# Revit family: RN 82230 Optipress-Aquaplus-Valvola di distribuzione
name_source: partatom
category: Rohrzubehör
units: mm (PartAtom-declared; Revit-internal decimal feet)

## family parameters
Arbeitsebenenbasiert = Nein
Beim Laden mit Abzugskörper schneiden = Nein
Bemaßung runder Anschluss = Durchmesser verwenden
Gemeinsam genutzt = Nein
Immer vertikal = Ja
Teiletyp = Ventil - Zerlegung in

## types (14) — shared parameters
1.010.00.2 Blattnummer der Richtlinie = 17
1.010.00.3 Ausgabedatum (Monat) der Richtlinie = 201601
1.010.00.4 Herstellername = R. Nussbaum AG
1.010.00.5 Revisionsdatum der Datei = 20190528
1.010.00.6 Webadresse des Herstellers = http://www.nussbaum.ch
1.100.00.3 Sortiernummer für Anzeigereihenfolge = 1
1.100.00.4 Produktbezeichnung = Absperrarmaturen
1.960/3L.00.8 Link (URL) = https://www.nussbaum.ch
17.700.00.4 Armaturentyp = 1
17.700.00.7 Maximale Betriebstemperatur TB [°C] = 90
17.700.00.8 Maximaler Betriebsdruck (Arbeitsdruck) ps [1.0 · 105 Pa] = 16
Connector Visibility = Nein
EnclosingSpace Visibility = Nein
Hersteller = R. Nussbauzm AG
URL = https://www.nussbaum.ch

## per-type parameters (varying)
- DN 20 1: 1.800.00.3 TGA-Nummer=00110000000000000000000000000200700000000000000001???00000; 1.810.00.3 Hersteller-Bestellnummer=82230.4; 1.810.00.4 DATANORM-Nummer=82230.4; 1.810.00.6 GTIN-Nummer=7612945729064; 17.700.00.30 Produktbeschreibung=82230.40, Optipress-Aquaplus-Batterieventil, ohne Anschlussverschraubung, DN=20; 17.700.00.5 Nennweite DN=20; 17.700.00.6 kvs-Wert [m3/h]=22.84; CONNECTOR0_DIAMETER_dX_0r=25 mm  [stored 0.082021 ft]; CONNECTOR0_dX_00=54 mm; CONNECTOR0_dX_01=31 mm; CONNECTOR0_ref_dX=31 mm; CONNECTOR1_DIAMETER_dX_0r=25 mm  [stored 0.082021 ft]; CONNECTOR1_dX_00=31 mm; CONNECTOR1_dX_01=54 mm; CONNECTOR1_ref_dX=31 mm; CONNECTOR2_DIAMETER_dZ_0r=25 mm  [stored 0.082021 ft]; CONNECTOR2_dZ_00=48 mm; CONNECTOR2_dZ_01=60 mm  [stored 0.19685 ft]; CONNECTOR2_ref_dZ=48 mm; Modell=82230.4; R. Nussbaum AG 82230.40 de Visibility=Ja; R. Nussbaum AG 82230.41 de Visibility=Nein; R. Nussbaum AG 82230.42 de Visibility=Nein; R. Nussbaum AG 82230.43 de Visibility=Nein; R. Nussbaum AG 82230.44 de Visibility=Nein; R. Nussbaum AG 82230.45 de Visibility=Nein; R. Nussbaum AG 82230.46 de Visibility=Nein; R. Nussbaum AG 82230.47 de Visibility=Nein; R. Nussbaum AG 82230.48 de Visibility=Nein; R. Nussbaum AG 82230.49 de Visibility=Nein; R. Nussbaum AG 82230.50 de Visibility=Nein; R. Nussbaum AG 82230.51 de Visibility=Nein; R. Nussbaum AG 82230.52 de Visibility=Nein; R. Nussbaum AG 82230.53 de Visibility=Nein; Typenkommentare=Optipress-Aquaplus-Valvola di distribuzioneDN 20 1
- DN 25: 1.800.00.3 TGA-Nummer=00110000000000000000000000000200700000000000000002???00000; 1.810.00.3 Hersteller-Bestellnummer=82230.41; 1.810.00.4 DATANORM-Nummer=82230.41; 1.810.00.6 GTIN-Nummer=7612945729118; 17.700.00.30 Produktbeschreibung=82230.41, Optipress-Aquaplus-Batterieventil, ohne Anschlussverschraubung, DN=25; 17.700.00.5 Nennweite DN=25; 17.700.00.6 kvs-Wert [m3/h]=22.84; CONNECTOR0_DIAMETER_dX_0r=25 mm  [stored 0.082021 ft]; CONNECTOR0_dX_00=54 mm; CONNECTOR0_dX_01=31 mm; CONNECTOR0_ref_dX=31 mm; CONNECTOR1_DIAMETER_dX_0r=25 mm  [stored 0.082021 ft]; CONNECTOR1_dX_00=31 mm; CONNECTOR1_dX_01=54 mm; CONNECTOR1_ref_dX=31 mm; CONNECTOR2_DIAMETER_dZ_0r=25 mm  [stored 0.082021 ft]; CONNECTOR2_dZ_00=48 mm; CONNECTOR2_dZ_01=60 mm  [stored 0.19685 ft]; CONNECTOR2_ref_dZ=48 mm; Modell=82230.41; R. Nussbaum AG 82230.40 de Visibility=Nein; R. Nussbaum AG 82230.41 de Visibility=Ja; R. Nussbaum AG 82230.42 de Visibility=Nein; R. Nussbaum AG 82230.43 de Visibility=Nein; R. Nussbaum AG 82230.44 de Visibility=Nein; R. Nussbaum AG 82230.45 de Visibility=Nein; R. Nussbaum AG 82230.46 de Visibility=Nein; R. Nussbaum AG 82230.47 de Visibility=Nein; R. Nussbaum AG 82230.48 de Visibility=Nein; R. Nussbaum AG 82230.49 de Visibility=Nein; R. Nussbaum AG 82230.50 de Visibility=Nein; R. Nussbaum AG 82230.51 de Visibility=Nein; R. Nussbaum AG 82230.52 de Visibility=Nein; R. Nussbaum AG 82230.53 de Visibility=Nein; Typenkommentare=Optipress-Aquaplus-Valvola di distribuzioneDN 25
- DN 20 2: 1.800.00.3 TGA-Nummer=00110000000000000000000000000200700000000000000003???00000; 1.810.00.3 Hersteller-Bestellnummer=82230.42; 1.810.00.4 DATANORM-Nummer=82230.42; 1.810.00.6 GTIN-Nummer=7612945729071; 17.700.00.30 Produktbeschreibung=82230.42, Optipress-Aquaplus-Batterieventil, ohne Anschlussverschraubung, DN=20; 17.700.00.5 Nennweite DN=20; 17.700.00.6 kvs-Wert [m3/h]=43.05; CONNECTOR0_DIAMETER_dX_0r=32 mm; CONNECTOR0_dX_00=56 mm; CONNECTOR0_dX_01=31 mm; CONNECTOR0_ref_dX=31 mm; CONNECTOR1_DIAMETER_dX_0r=32 mm; CONNECTOR1_dX_00=31 mm; CONNECTOR1_dX_01=56 mm; CONNECTOR1_ref_dX=31 mm; CONNECTOR2_DIAMETER_dZ_0r=25 mm  [stored 0.082021 ft]; CONNECTOR2_dZ_00=50 mm  [stored 0.164042 ft]; CONNECTOR2_dZ_01=62 mm  [stored 0.203412 ft]; CONNECTOR2_ref_dZ=50 mm  [stored 0.164042 ft]; Modell=82230.42; R. Nussbaum AG 82230.40 de Visibility=Nein; R. Nussbaum AG 82230.41 de Visibility=Nein; R. Nussbaum AG 82230.42 de Visibility=Ja; R. Nussbaum AG 82230.43 de Visibility=Nein; R. Nussbaum AG 82230.44 de Visibility=Nein; R. Nussbaum AG 82230.45 de Visibility=Nein; R. Nussbaum AG 82230.46 de Visibility=Nein; R. Nussbaum AG 82230.47 de Visibility=Nein; R. Nussbaum AG 82230.48 de Visibility=Nein; R. Nussbaum AG 82230.49 de Visibility=Nein; R. Nussbaum AG 82230.50 de Visibility=Nein; R. Nussbaum AG 82230.51 de Visibility=Nein; R. Nussbaum AG 82230.52 de Visibility=Nein; R. Nussbaum AG 82230.53 de Visibility=Nein; Typenkommentare=Optipress-Aquaplus-Valvola di distribuzioneDN 20 2
- DN 25 1: 1.800.00.3 TGA-Nummer=00110000000000000000000000000200700000000000000004???00000; 1.810.00.3 Hersteller-Bestellnummer=82230.43; 1.810.00.4 DATANORM-Nummer=82230.43; 1.810.00.6 GTIN-Nummer=7612945729125; 17.700.00.30 Produktbeschreibung=82230.43, Optipress-Aquaplus-Batterieventil, ohne Anschlussverschraubung, DN=25; 17.700.00.5 Nennweite DN=25; 17.700.00.6 kvs-Wert [m3/h]=43.05; CONNECTOR0_DIAMETER_dX_0r=32 mm; CONNECTOR0_dX_00=56 mm; CONNECTOR0_dX_01=31 mm; CONNECTOR0_ref_dX=31 mm; CONNECTOR1_DIAMETER_dX_0r=32 mm; CONNECTOR1_dX_00=31 mm; CONNECTOR1_dX_01=56 mm; CONNECTOR1_ref_dX=31 mm; CONNECTOR2_DIAMETER_dZ_0r=25 mm  [stored 0.082021 ft]; CONNECTOR2_dZ_00=50 mm  [stored 0.164042 ft]; CONNECTOR2_dZ_01=62 mm  [stored 0.203412 ft]; CONNECTOR2_ref_dZ=50 mm  [stored 0.164042 ft]; Modell=82230.43; R. Nussbaum AG 82230.40 de Visibility=Nein; R. Nussbaum AG 82230.41 de Visibility=Nein; R. Nussbaum AG 82230.42 de Visibility=Nein; R. Nussbaum AG 82230.43 de Visibility=Ja; R. Nussbaum AG 82230.44 de Visibility=Nein; R. Nussbaum AG 82230.45 de Visibility=Nein; R. Nussbaum AG 82230.46 de Visibility=Nein; R. Nussbaum AG 82230.47 de Visibility=Nein; R. Nussbaum AG 82230.48 de Visibility=Nein; R. Nussbaum AG 82230.49 de Visibility=Nein; R. Nussbaum AG 82230.50 de Visibility=Nein; R. Nussbaum AG 82230.51 de Visibility=Nein; R. Nussbaum AG 82230.52 de Visibility=Nein; R. Nussbaum AG 82230.53 de Visibility=Nein; Typenkommentare=Optipress-Aquaplus-Valvola di distribuzioneDN 25 1
- DN 32: 1.800.00.3 TGA-Nummer=00110000000000000000000000000200700000000000000005???00000; 1.810.00.3 Hersteller-Bestellnummer=82230.44; 1.810.00.4 DATANORM-Nummer=82230.44; 1.810.00.6 GTIN-Nummer=7612945729088; 17.700.00.30 Produktbeschreibung=82230.44, Optipress-Aquaplus-Batterieventil, ohne Anschlussverschraubung, DN=32; 17.700.00.5 Nennweite DN=32; 17.700.00.6 kvs-Wert [m3/h]=43.05; CONNECTOR0_DIAMETER_dX_0r=32 mm; CONNECTOR0_dX_00=56 mm; CONNECTOR0_dX_01=31 mm; CONNECTOR0_ref_dX=31 mm; CONNECTOR1_DIAMETER_dX_0r=32 mm; CONNECTOR1_dX_00=31 mm; CONNECTOR1_dX_01=56 mm; CONNECTOR1_ref_dX=31 mm; CONNECTOR2_DIAMETER_dZ_0r=32 mm; CONNECTOR2_dZ_00=49 mm; CONNECTOR2_dZ_01=62 mm  [stored 0.203412 ft]; CONNECTOR2_ref_dZ=49 mm; Modell=82230.44; R. Nussbaum AG 82230.40 de Visibility=Nein; R. Nussbaum AG 82230.41 de Visibility=Nein; R. Nussbaum AG 82230.42 de Visibility=Nein; R. Nussbaum AG 82230.43 de Visibility=Nein; R. Nussbaum AG 82230.44 de Visibility=Ja; R. Nussbaum AG 82230.45 de Visibility=Nein; R. Nussbaum AG 82230.46 de Visibility=Nein; R. Nussbaum AG 82230.47 de Visibility=Nein; R. Nussbaum AG 82230.48 de Visibility=Nein; R. Nussbaum AG 82230.49 de Visibility=Nein; R. Nussbaum AG 82230.50 de Visibility=Nein; R. Nussbaum AG 82230.51 de Visibility=Nein; R. Nussbaum AG 82230.52 de Visibility=Nein; R. Nussbaum AG 82230.53 de Visibility=Nein; Typenkommentare=Optipress-Aquaplus-Valvola di distribuzioneDN 32
- DN 20: 1.800.00.3 TGA-Nummer=00110000000000000000000000000200700000000000000006???00000; 1.810.00.3 Hersteller-Bestellnummer=82230.45; 1.810.00.4 DATANORM-Nummer=82230.45; 1.810.00.6 GTIN-Nummer=7612945729095; 17.700.00.30 Produktbeschreibung=82230.45, Optipress-Aquaplus-Batterieventil, ohne Anschlussverschraubung, DN=20; 17.700.00.5 Nennweite DN=20; 17.700.00.6 kvs-Wert [m3/h]=36.27; CONNECTOR0_DIAMETER_dX_0r=40 mm; CONNECTOR0_dX_00=66 mm  [stored 0.216535 ft]; CONNECTOR0_dX_01=30 mm  [stored 0.0984252 ft]; CONNECTOR0_ref_dX=30 mm  [stored 0.0984252 ft]; CONNECTOR1_DIAMETER_dX_0r=40 mm; CONNECTOR1_dX_00=30 mm  [stored 0.0984252 ft]; CONNECTOR1_dX_01=66 mm  [stored 0.216535 ft]; CONNECTOR1_ref_dX=30 mm  [stored 0.0984252 ft]; CONNECTOR2_DIAMETER_dZ_0r=31 mm; CONNECTOR2_dZ_00=52 mm; CONNECTOR2_dZ_01=65 mm; CONNECTOR2_ref_dZ=52 mm; Modell=82230.45; R. Nussbaum AG 82230.40 de Visibility=Nein; R. Nussbaum AG 82230.41 de Visibility=Nein; R. Nussbaum AG 82230.42 de Visibility=Nein; R. Nussbaum AG 82230.43 de Visibility=Nein; R. Nussbaum AG 82230.44 de Visibility=Nein; R. Nussbaum AG 82230.45 de Visibility=Ja; R. Nussbaum AG 82230.46 de Visibility=Nein; R. Nussbaum AG 82230.47 de Visibility=Nein; R. Nussbaum AG 82230.48 de Visibility=Nein; R. Nussbaum AG 82230.49 de Visibility=Nein; R. Nussbaum AG 82230.50 de Visibility=Nein; R. Nussbaum AG 82230.51 de Visibility=Nein; R. Nussbaum AG 82230.52 de Visibility=Nein; R. Nussbaum AG 82230.53 de Visibility=Nein; Typenkommentare=Optipress-Aquaplus-Valvola di distribuzioneDN 20
- DN 25 3: 1.800.00.3 TGA-Nummer=00110000000000000000000000000200700000000000000007???00000; 1.810.00.3 Hersteller-Bestellnummer=82230.46; 1.810.00.4 DATANORM-Nummer=82230.46; 1.810.00.6 GTIN-Nummer=7612945729132; 17.700.00.30 Produktbeschreibung=82230.46, Optipress-Aquaplus-Batterieventil, ohne Anschlussverschraubung, DN=25; 17.700.00.5 Nennweite DN=25; 17.700.00.6 kvs-Wert [m3/h]=36.27; CONNECTOR0_DIAMETER_dX_0r=40 mm; CONNECTOR0_dX_00=66 mm  [stored 0.216535 ft]; CONNECTOR0_dX_01=30 mm  [stored 0.0984252 ft]; CONNECTOR0_ref_dX=30 mm  [stored 0.0984252 ft]; CONNECTOR1_DIAMETER_dX_0r=40 mm; CONNECTOR1_dX_00=30 mm  [stored 0.0984252 ft]; CONNECTOR1_dX_01=66 mm  [stored 0.216535 ft]; CONNECTOR1_ref_dX=30 mm  [stored 0.0984252 ft]; CONNECTOR2_DIAMETER_dZ_0r=32 mm; CONNECTOR2_dZ_00=52 mm; CONNECTOR2_dZ_01=65 mm; CONNECTOR2_ref_dZ=52 mm; Modell=82230.46; R. Nussbaum AG 82230.40 de Visibility=Nein; R. Nussbaum AG 82230.41 de Visibility=Nein; R. Nussbaum AG 82230.42 de Visibility=Nein; R. Nussbaum AG 82230.43 de Visibility=Nein; R. Nussbaum AG 82230.44 de Visibility=Nein; R. Nussbaum AG 82230.45 de Visibility=Nein; R. Nussbaum AG 82230.46 de Visibility=Ja; R. Nussbaum AG 82230.47 de Visibility=Nein; R. Nussbaum AG 82230.48 de Visibility=Nein; R. Nussbaum AG 82230.49 de Visibility=Nein; R. Nussbaum AG 82230.50 de Visibility=Nein; R. Nussbaum AG 82230.51 de Visibility=Nein; R. Nussbaum AG 82230.52 de Visibility=Nein; R. Nussbaum AG 82230.53 de Visibility=Nein; Typenkommentare=Optipress-Aquaplus-Valvola di distribuzioneDN 25 3
- DN 32 2: 1.800.00.3 TGA-Nummer=00110000000000000000000000000200700000000000000008???00000; 1.810.00.3 Hersteller-Bestellnummer=82230.47; 1.810.00.4 DATANORM-Nummer=82230.47; 1.810.00.6 GTIN-Nummer=7612945729149; 17.700.00.30 Produktbeschreibung=82230.47, Optipress-Aquaplus-Batterieventil, ohne Anschlussverschraubung, DN=32; 17.700.00.5 Nennweite DN=32; 17.700.00.6 kvs-Wert [m3/h]=36.27; CONNECTOR0_DIAMETER_dX_0r=40 mm; CONNECTOR0_dX_00=66 mm  [stored 0.216535 ft]; CONNECTOR0_dX_01=30 mm  [stored 0.0984252 ft]; CONNECTOR0_ref_dX=30 mm  [stored 0.0984252 ft]; CONNECTOR1_DIAMETER_dX_0r=40 mm; CONNECTOR1_dX_00=30 mm  [stored 0.0984252 ft]; CONNECTOR1_dX_01=66 mm  [stored 0.216535 ft]; CONNECTOR1_ref_dX=30 mm  [stored 0.0984252 ft]; CONNECTOR2_DIAMETER_dZ_0r=32 mm; CONNECTOR2_dZ_00=52 mm; CONNECTOR2_dZ_01=65 mm; CONNECTOR2_ref_dZ=52 mm; Modell=82230.47; R. Nussbaum AG 82230.40 de Visibility=Nein; R. Nussbaum AG 82230.41 de Visibility=Nein; R. Nussbaum AG 82230.42 de Visibility=Nein; R. Nussbaum AG 82230.43 de Visibility=Nein; R. Nussbaum AG 82230.44 de Visibility=Nein; R. Nussbaum AG 82230.45 de Visibility=Nein; R. Nussbaum AG 82230.46 de Visibility=Nein; R. Nussbaum AG 82230.47 de Visibility=Ja; R. Nussbaum AG 82230.48 de Visibility=Nein; R. Nussbaum AG 82230.49 de Visibility=Nein; R. Nussbaum AG 82230.50 de Visibility=Nein; R. Nussbaum AG 82230.51 de Visibility=Nein; R. Nussbaum AG 82230.52 de Visibility=Nein; R. Nussbaum AG 82230.53 de Visibility=Nein; Typenkommentare=Optipress-Aquaplus-Valvola di distribuzioneDN 32 2
- DN 40 1: 1.800.00.3 TGA-Nummer=00110000000000000000000000000200700000000000000009???00000; 1.810.00.3 Hersteller-Bestellnummer=82230.48; 1.810.00.4 DATANORM-Nummer=82230.48; 1.810.00.6 GTIN-Nummer=7612945727206; 17.700.00.30 Produktbeschreibung=82230.48, Optipress-Aquaplus-Batterieventil, ohne Anschlussverschraubung, DN=40; 17.700.00.5 Nennweite DN=40; 17.700.00.6 kvs-Wert [m3/h]=36.27; CONNECTOR0_DIAMETER_dX_0r=40 mm; CONNECTOR0_dX_00=66 mm  [stored 0.216535 ft]; CONNECTOR0_dX_01=30 mm  [stored 0.0984252 ft]; CONNECTOR0_ref_dX=30 mm  [stored 0.0984252 ft]; CONNECTOR1_DIAMETER_dX_0r=40 mm; CONNECTOR1_dX_00=30 mm  [stored 0.0984252 ft]; CONNECTOR1_dX_01=66 mm  [stored 0.216535 ft]; CONNECTOR1_ref_dX=30 mm  [stored 0.0984252 ft]; CONNECTOR2_DIAMETER_dZ_0r=40 mm; CONNECTOR2_dZ_00=52 mm; CONNECTOR2_dZ_01=65 mm; CONNECTOR2_ref_dZ=52 mm; Modell=82230.48; R. Nussbaum AG 82230.40 de Visibility=Nein; R. Nussbaum AG 82230.41 de Visibility=Nein; R. Nussbaum AG 82230.42 de Visibility=Nein; R. Nussbaum AG 82230.43 de Visibility=Nein; R. Nussbaum AG 82230.44 de Visibility=Nein; R. Nussbaum AG 82230.45 de Visibility=Nein; R. Nussbaum AG 82230.46 de Visibility=Nein; R. Nussbaum AG 82230.47 de Visibility=Nein; R. Nussbaum AG 82230.48 de Visibility=Ja; R. Nussbaum AG 82230.49 de Visibility=Nein; R. Nussbaum AG 82230.50 de Visibility=Nein; R. Nussbaum AG 82230.51 de Visibility=Nein; R. Nussbaum AG 82230.52 de Visibility=Nein; R. Nussbaum AG 82230.53 de Visibility=Nein; Typenkommentare=Optipress-Aquaplus-Valvola di distribuzioneDN 40 1
- DN 20 3: 1.800.00.3 TGA-Nummer=00110000000000000000000000000200700000000000000010???00000; 1.810.00.3 Hersteller-Bestellnummer=82230.49; 1.810.00.4 DATANORM-Nummer=82230.49; 1.810.00.6 GTIN-Nummer=7612945729101; 17.700.00.30 Produktbeschreibung=82230.49, Optipress-Aquaplus-Batterieventil, ohne Anschlussverschraubung, DN=20; 17.700.00.5 Nennweite DN=20; 17.700.00.6 kvs-Wert [m3/h]=33.26; CONNECTOR0_DIAMETER_dX_0r=50 mm  [stored 0.164042 ft]; CONNECTOR0_dX_00=80 mm; CONNECTOR0_dX_01=40 mm; CONNECTOR0_ref_dX=40 mm; CONNECTOR1_DIAMETER_dX_0r=50 mm  [stored 0.164042 ft]; CONNECTOR1_dX_00=40 mm; CONNECTOR1_dX_01=80 mm; CONNECTOR1_ref_dX=40 mm; CONNECTOR2_DIAMETER_dZ_0r=52 mm; CONNECTOR2_dZ_00=60 mm  [stored 0.19685 ft]; CONNECTOR2_dZ_01=73 mm; CONNECTOR2_ref_dZ=60 mm  [stored 0.19685 ft]; Modell=82230.49; R. Nussbaum AG 82230.40 de Visibility=Nein; R. Nussbaum AG 82230.41 de Visibility=Nein; R. Nussbaum AG 82230.42 de Visibility=Nein; R. Nussbaum AG 82230.43 de Visibility=Nein; R. Nussbaum AG 82230.44 de Visibility=Nein; R. Nussbaum AG 82230.45 de Visibility=Nein; R. Nussbaum AG 82230.46 de Visibility=Nein; R. Nussbaum AG 82230.47 de Visibility=Nein; R. Nussbaum AG 82230.48 de Visibility=Nein; R. Nussbaum AG 82230.49 de Visibility=Ja; R. Nussbaum AG 82230.50 de Visibility=Nein; R. Nussbaum AG 82230.51 de Visibility=Nein; R. Nussbaum AG 82230.52 de Visibility=Nein; R. Nussbaum AG 82230.53 de Visibility=Nein; Typenkommentare=Optipress-Aquaplus-Valvola di distribuzioneDN 20 3
- DN 25 2: 1.800.00.3 TGA-Nummer=00110000000000000000000000000200700000000000000011???00000; 1.810.00.3 Hersteller-Bestellnummer=82230.5; 1.810.00.4 DATANORM-Nummer=82230.5; 1.810.00.6 GTIN-Nummer=7612945729156; 17.700.00.30 Produktbeschreibung=82230.50, Optipress-Aquaplus-Batterieventil, ohne Anschlussverschraubung, DN=25; 17.700.00.5 Nennweite DN=25; 17.700.00.6 kvs-Wert [m3/h]=33.26; CONNECTOR0_DIAMETER_dX_0r=50 mm  [stored 0.164042 ft]; CONNECTOR0_dX_00=80 mm; CONNECTOR0_dX_01=40 mm; CONNECTOR0_ref_dX=40 mm; CONNECTOR1_DIAMETER_dX_0r=50 mm  [stored 0.164042 ft]; CONNECTOR1_dX_00=40 mm; CONNECTOR1_dX_01=80 mm; CONNECTOR1_ref_dX=40 mm; CONNECTOR2_DIAMETER_dZ_0r=32 mm; CONNECTOR2_dZ_00=60 mm  [stored 0.19685 ft]; CONNECTOR2_dZ_01=73 mm; CONNECTOR2_ref_dZ=60 mm  [stored 0.19685 ft]; Modell=82230.5; R. Nussbaum AG 82230.40 de Visibility=Nein; R. Nussbaum AG 82230.41 de Visibility=Nein; R. Nussbaum AG 82230.42 de Visibility=Nein; R. Nussbaum AG 82230.43 de Visibility=Nein; R. Nussbaum AG 82230.44 de Visibility=Nein; R. Nussbaum AG 82230.45 de Visibility=Nein; R. Nussbaum AG 82230.46 de Visibility=Nein; R. Nussbaum AG 82230.47 de Visibility=Nein; R. Nussbaum AG 82230.48 de Visibility=Nein; R. Nussbaum AG 82230.49 de Visibility=Nein; R. Nussbaum AG 82230.50 de Visibility=Ja; R. Nussbaum AG 82230.51 de Visibility=Nein; R. Nussbaum AG 82230.52 de Visibility=Nein; R. Nussbaum AG 82230.53 de Visibility=Nein; Typenkommentare=Optipress-Aquaplus-Valvola di distribuzioneDN 25 2
- DN 32 1: 1.800.00.3 TGA-Nummer=00110000000000000000000000000200700000000000000012???00000; 1.810.00.3 Hersteller-Bestellnummer=82230.51; 1.810.00.4 DATANORM-Nummer=82230.51; 1.810.00.6 GTIN-Nummer=7612945729163; 17.700.00.30 Produktbeschreibung=82230.51, Optipress-Aquaplus-Batterieventil, ohne Anschlussverschraubung, DN=32; 17.700.00.5 Nennweite DN=32; 17.700.00.6 kvs-Wert [m3/h]=33.26; CONNECTOR0_DIAMETER_dX_0r=50 mm  [stored 0.164042 ft]; CONNECTOR0_dX_00=80 mm; CONNECTOR0_dX_01=40 mm; CONNECTOR0_ref_dX=40 mm; CONNECTOR1_DIAMETER_dX_0r=50 mm  [stored 0.164042 ft]; CONNECTOR1_dX_00=40 mm; CONNECTOR1_dX_01=80 mm; CONNECTOR1_ref_dX=40 mm; CONNECTOR2_DIAMETER_dZ_0r=32 mm; CONNECTOR2_dZ_00=60 mm  [stored 0.19685 ft]; CONNECTOR2_dZ_01=73 mm; CONNECTOR2_ref_dZ=60 mm  [stored 0.19685 ft]; Modell=82230.51; R. Nussbaum AG 82230.40 de Visibility=Nein; R. Nussbaum AG 82230.41 de Visibility=Nein; R. Nussbaum AG 82230.42 de Visibility=Nein; R. Nussbaum AG 82230.43 de Visibility=Nein; R. Nussbaum AG 82230.44 de Visibility=Nein; R. Nussbaum AG 82230.45 de Visibility=Nein; R. Nussbaum AG 82230.46 de Visibility=Nein; R. Nussbaum AG 82230.47 de Visibility=Nein; R. Nussbaum AG 82230.48 de Visibility=Nein; R. Nussbaum AG 82230.49 de Visibility=Nein; R. Nussbaum AG 82230.50 de Visibility=Nein; R. Nussbaum AG 82230.51 de Visibility=Ja; R. Nussbaum AG 82230.52 de Visibility=Nein; R. Nussbaum AG 82230.53 de Visibility=Nein; Typenkommentare=Optipress-Aquaplus-Valvola di distribuzioneDN 32 1
- DN 40: 1.800.00.3 TGA-Nummer=00110000000000000000000000000200700000000000000013???00000; 1.810.00.3 Hersteller-Bestellnummer=82230.52; 1.810.00.4 DATANORM-Nummer=82230.52; 1.810.00.6 GTIN-Nummer=7612945727213; 17.700.00.30 Produktbeschreibung=82230.52, Optipress-Aquaplus-Batterieventil, ohne Anschlussverschraubung, DN=40; 17.700.00.5 Nennweite DN=40; 17.700.00.6 kvs-Wert [m3/h]=82.84; CONNECTOR0_DIAMETER_dX_0r=50 mm  [stored 0.164042 ft]; CONNECTOR0_dX_00=80 mm; CONNECTOR0_dX_01=40 mm; CONNECTOR0_ref_dX=40 mm; CONNECTOR1_DIAMETER_dX_0r=50 mm  [stored 0.164042 ft]; CONNECTOR1_dX_00=40 mm; CONNECTOR1_dX_01=80 mm; CONNECTOR1_ref_dX=40 mm; CONNECTOR2_DIAMETER_dZ_0r=40 mm; CONNECTOR2_dZ_00=60 mm  [stored 0.19685 ft]; CONNECTOR2_dZ_01=73 mm; CONNECTOR2_ref_dZ=60 mm  [stored 0.19685 ft]; Modell=82230.52; R. Nussbaum AG 82230.40 de Visibility=Nein; R. Nussbaum AG 82230.41 de Visibility=Nein; R. Nussbaum AG 82230.42 de Visibility=Nein; R. Nussbaum AG 82230.43 de Visibility=Nein; R. Nussbaum AG 82230.44 de Visibility=Nein; R. Nussbaum AG 82230.45 de Visibility=Nein; R. Nussbaum AG 82230.46 de Visibility=Nein; R. Nussbaum AG 82230.47 de Visibility=Nein; R. Nussbaum AG 82230.48 de Visibility=Nein; R. Nussbaum AG 82230.49 de Visibility=Nein; R. Nussbaum AG 82230.50 de Visibility=Nein; R. Nussbaum AG 82230.51 de Visibility=Nein; R. Nussbaum AG 82230.52 de Visibility=Ja; R. Nussbaum AG 82230.53 de Visibility=Nein; Typenkommentare=Optipress-Aquaplus-Valvola di distribuzioneDN 40
- DN 50: 1.800.00.3 TGA-Nummer=00110000000000000000000000000200700000000000000014???00000; 1.810.00.3 Hersteller-Bestellnummer=82230.53; 1.810.00.4 DATANORM-Nummer=82230.53; 1.810.00.6 GTIN-Nummer=7612945727220; 17.700.00.30 Produktbeschreibung=82230.53, Optipress-Aquaplus-Batterieventil, ohne Anschlussverschraubung, DN=50; 17.700.00.5 Nennweite DN=50; 17.700.00.6 kvs-Wert [m3/h]=82.84; CONNECTOR0_DIAMETER_dX_0r=50 mm  [stored 0.164042 ft]; CONNECTOR0_dX_00=80 mm; CONNECTOR0_dX_01=40 mm; CONNECTOR0_ref_dX=40 mm; CONNECTOR1_DIAMETER_dX_0r=50 mm  [stored 0.164042 ft]; CONNECTOR1_dX_00=40 mm; CONNECTOR1_dX_01=80 mm; CONNECTOR1_ref_dX=40 mm; CONNECTOR2_DIAMETER_dZ_0r=40 mm; CONNECTOR2_dZ_00=60 mm  [stored 0.19685 ft]; CONNECTOR2_dZ_01=73 mm; CONNECTOR2_ref_dZ=60 mm  [stored 0.19685 ft]; Modell=82230.53; R. Nussbaum AG 82230.40 de Visibility=Nein; R. Nussbaum AG 82230.41 de Visibility=Nein; R. Nussbaum AG 82230.42 de Visibility=Nein; R. Nussbaum AG 82230.43 de Visibility=Nein; R. Nussbaum AG 82230.44 de Visibility=Nein; R. Nussbaum AG 82230.45 de Visibility=Nein; R. Nussbaum AG 82230.46 de Visibility=Nein; R. Nussbaum AG 82230.47 de Visibility=Nein; R. Nussbaum AG 82230.48 de Visibility=Nein; R. Nussbaum AG 82230.49 de Visibility=Nein; R. Nussbaum AG 82230.50 de Visibility=Nein; R. Nussbaum AG 82230.51 de Visibility=Nein; R. Nussbaum AG 82230.52 de Visibility=Nein; R. Nussbaum AG 82230.53 de Visibility=Ja; Typenkommentare=Optipress-Aquaplus-Valvola di distribuzioneDN 50

note: [stored X ft] marks values corroborated as IEEE doubles in the binary element streams (Revit-internal decimal feet)

## geometry (parser evidence)
native form markers: Sweep x1
no freeform markers — native parametric forms only
